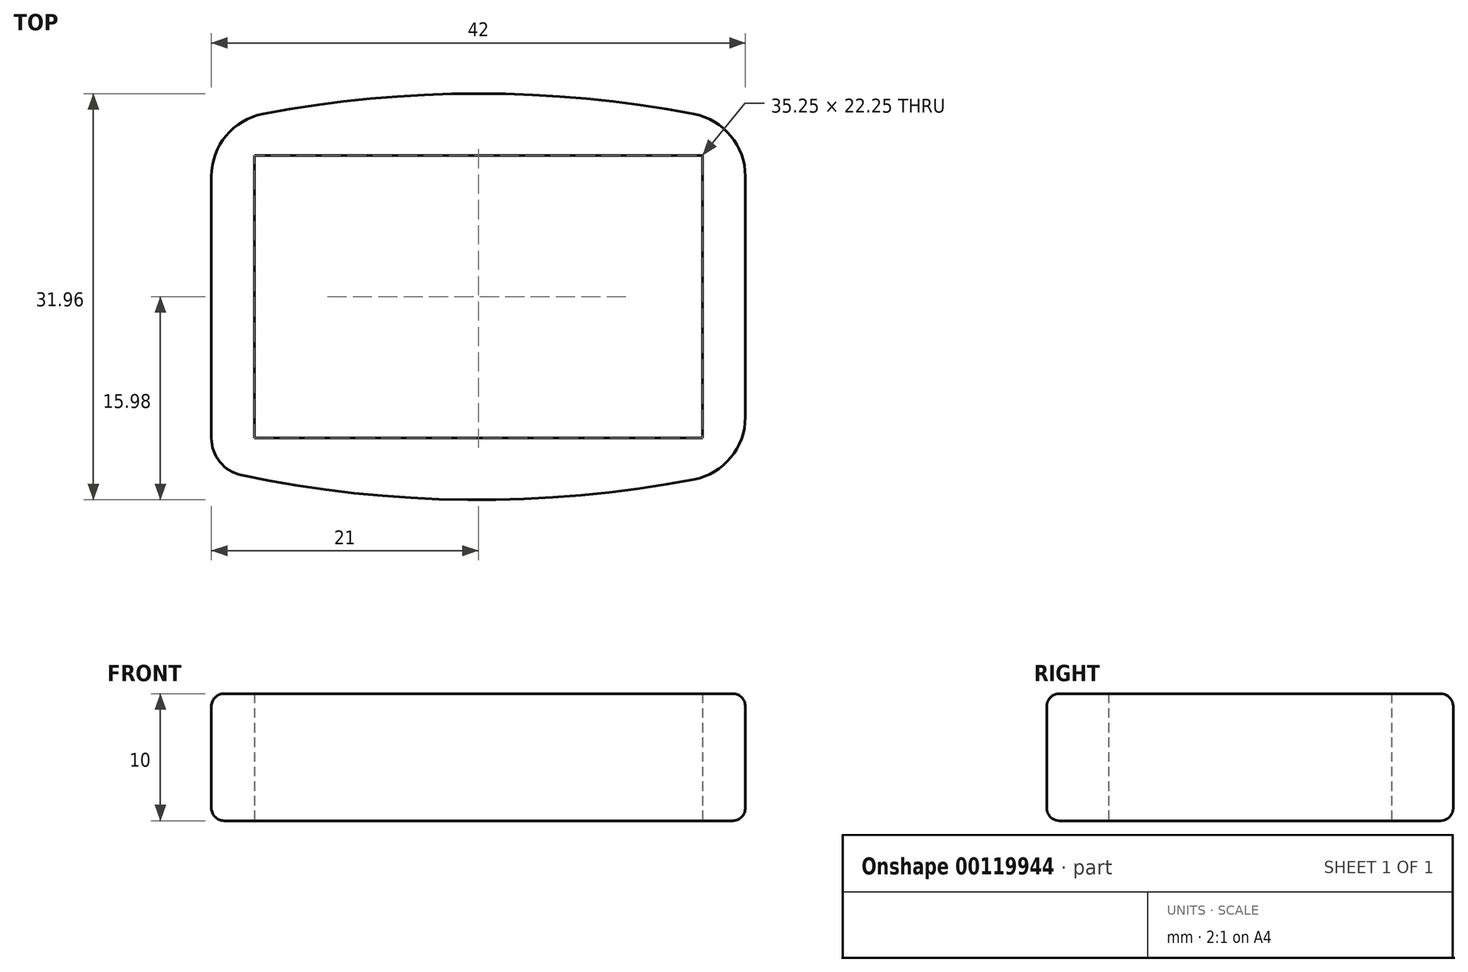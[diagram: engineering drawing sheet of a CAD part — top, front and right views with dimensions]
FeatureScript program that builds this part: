
annotation { "Feature Type Name" : "Feature", "Feature Type Description" : "" }
export const myFeature = defineFeature(function(context is Context, id is Id, definition is map)
    precondition{}
    {
        {
            var Q0;
            Q0=qCreatedBy(makeId("Top.planeOp"),FACE);
            var sketch = newSketch(context, id + "F0", { "sketchPlane" : qUnion([Q0])});
            skLineSegment(sketch, "E0.bottom", {"start": v(17.62, 11.12) * mm, "end": v(-17.62, 11.12) * mm});
            skLineSegment(sketch, "E0.top", {"start": v(17.62, -11.12) * mm, "end": v(-17.62, -11.12) * mm});
            skLineSegment(sketch, "E0.left", {"start": v(17.62, 11.12) * mm, "end": v(17.62, -11.12) * mm});
            skLineSegment(sketch, "E0.right", {"start": v(-17.62, 11.12) * mm, "end": v(-17.62, -11.12) * mm});
            skPoint(sketch, "E0.middle", {"position": v(0, 0) * mm});
            skLineSegment(sketch, "E1.left", {"start": v(21, 9.46) * mm, "end": v(21, -9.46) * mm});
            skLineSegment(sketch, "E1.right", {"start": v(-21, 9.46) * mm, "end": v(-21, -11.1) * mm});
            skArc(sketch, "E2", {"start": v(16.94, 14.38) * mm, "mid": v(0, 15.98) * mm, "end": v(-16.94, 14.38) * mm});
            skArc(sketch, "E3", {"start": v(-18.62, -14.04) * mm, "mid": v(-0.86, -15.98) * mm, "end": v(16.94, -14.38) * mm});
            skPoint(sketch, "E4.visualSharp", {"position": v(-21, 13.5) * mm});
            skArc(sketch, "E4.filletArc", {"start": v(-16.94, 14.38) * mm, "mid": v(-19.85, 12.65) * mm, "end": v(-21, 9.46) * mm});
            skPoint(sketch, "E5.visualSharp", {"position": v(21, 13.5) * mm});
            skArc(sketch, "E5.filletArc", {"start": v(21, 9.46) * mm, "mid": v(19.85, 12.65) * mm, "end": v(16.94, 14.38) * mm});
            skPoint(sketch, "E6.visualSharp", {"position": v(21, -13.5) * mm});
            skArc(sketch, "E6.filletArc", {"start": v(16.94, -14.38) * mm, "mid": v(19.85, -12.65) * mm, "end": v(21, -9.46) * mm});
            skPoint(sketch, "E7.visualSharp", {"position": v(-21, -13.5) * mm});
            skArc(sketch, "E7.filletArc", {"start": v(-21, -11.1) * mm, "mid": v(-20.33, -13) * mm, "end": v(-18.62, -14.04) * mm});
            skSolve(sketch);
        }
        {
            var Q0;
            Q0=makeQuery(id+"F0.imprint","IMPRINT",FACE,{"disambiguationData":[TD([[makeQuery(id+"F0.imprint","IMPRINT",EDGE,{"derivedFrom":sQuery(id+"F0.wireOp",EDGE,"E0.bottom")}),-1.0]])]});
            extrude(context, id + "F1", {"entities" : qUnion([Q0]), "depth" : 10 * mm});
        }
        {
            var Q0;
            Q0=makeQuery(id+"F1.opExtrude","CAP_EDGE",EDGE,{"disambiguationData":[OSD([sQuery(id+"F0.wireOp",EDGE,"E5.filletArc")])],"isStart":false});
            var Q1;
            Q1=makeQuery(id+"F1.opExtrude","CAP_EDGE",EDGE,{"disambiguationData":[OSD([sQuery(id+"F0.wireOp",EDGE,"E5.filletArc")])],"isStart":true});
            fillet(context, id + "F2", {"entities" : qUnion([Q0, Q1]), "radius" : 1 * mm, "tangentPropagation" : true, "allowEdgeOverflow" : false});
        }
    });
